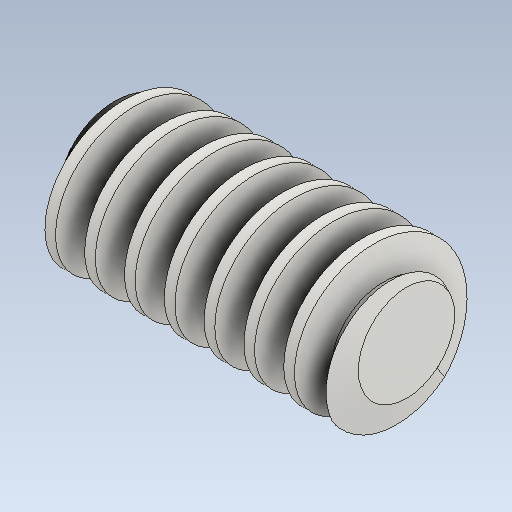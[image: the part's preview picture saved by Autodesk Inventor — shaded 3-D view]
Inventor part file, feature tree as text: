
AUTODESK INVENTOR PART (.ipt)
format: ipt  version: 2020.3 (Build 243373000, 373)  size: 429,056 bytes
history: native  units: mm (DEFAULTED — no unit token found)
features: other x6, chamfer x2, pattern_circular x2, extrude x1, sketch x1
ambient origin geometry x6: Origin, XZ Plane, X Axis, Y Axis, Z Axis, Center Point
bodies: Solid1 (feature_tree)
feature tree (12):
  extrude  "Base Body"  Depth=10.0mm
  chamfer  "Chamfer1"  Distance=60.0mm
  chamfer  "Chamfer2"  [1 undecoded]
  other  "Tooth Sketch"
  other  "Left Tooth"
  pattern_circular  "Left Tooth Pattern"  [2 undecoded]
  other  "Tooth"
  pattern_circular  "Tooth Pattern"  [2 undecoded]
  other  "Base Body Sketch"
  sketch  "Sketch5"  dims[d4=40.0mm d5=30.319017mm d6=60.0mm d7=0.0mm d8=2.023124mm d9=5.558486mm d10=2.023124mm d11=5.558486mm d12=19.198622mm d14=3.1425mm d24=19.198622mm d25=35.71875mm d26=1.984375mm d27=9.601022mm d28=12.632924mm d29=15.311103mm d30=7.9375mm d31=10.0mm d32=100.0mm d33=0.0mm d34=90.0deg d35=90.0deg d36=0.0mm d37=0.0mm d43=10.0mm d45=360.0deg d46=45.0deg d47=45.0deg d49=0.0mm d53=0.0mm d54=63.164618mm d55=0.0mm d56=0.0mm d57=25.265847mm d58=25.4mm d59=0.0mm d60=7.9375mm d61=25.4mm d62=100.0mm d63=0.0mm d64=90.0deg d65=90.0deg d66=0.0mm d67=0.0mm d68=10.0mm d69=10.0mm d70=360.0deg d72=10.0mm d74=10.0mm d75=10.0mm d76=0.0mm d77=63.164618mm]
  other  "Srf1"
  other  "Pitch Diameter"
note: 5 required parameter values undecoded (feature->parameter linkage not recoverable at this tier; creation-order binding heuristic only, values carry confidence <= 0.55)
